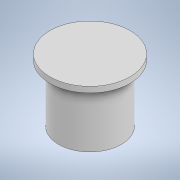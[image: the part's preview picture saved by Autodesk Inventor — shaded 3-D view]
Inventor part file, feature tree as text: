
AUTODESK INVENTOR PART (.ipt)
format: ipt  version: 2022 (Build 260153000, 153)  size: 109,568 bytes
history: native  units: mm
features: extrude x2, sketch x2, other x1
ambient origin geometry x8: Origin, YZ Plane, XZ Plane, XY Plane, X Axis, Y Axis, Z Axis, Center Point
bodies: Body1 (feature_tree)
feature tree (5):
  other  "Bryła1"
  extrude  "Wyciągnięcie proste1"  Depth=22.0mm
  extrude  "Wyciągnięcie proste2"  Depth=2.0mm
  sketch  "Szkic1"
  sketch  "Szkic2"
